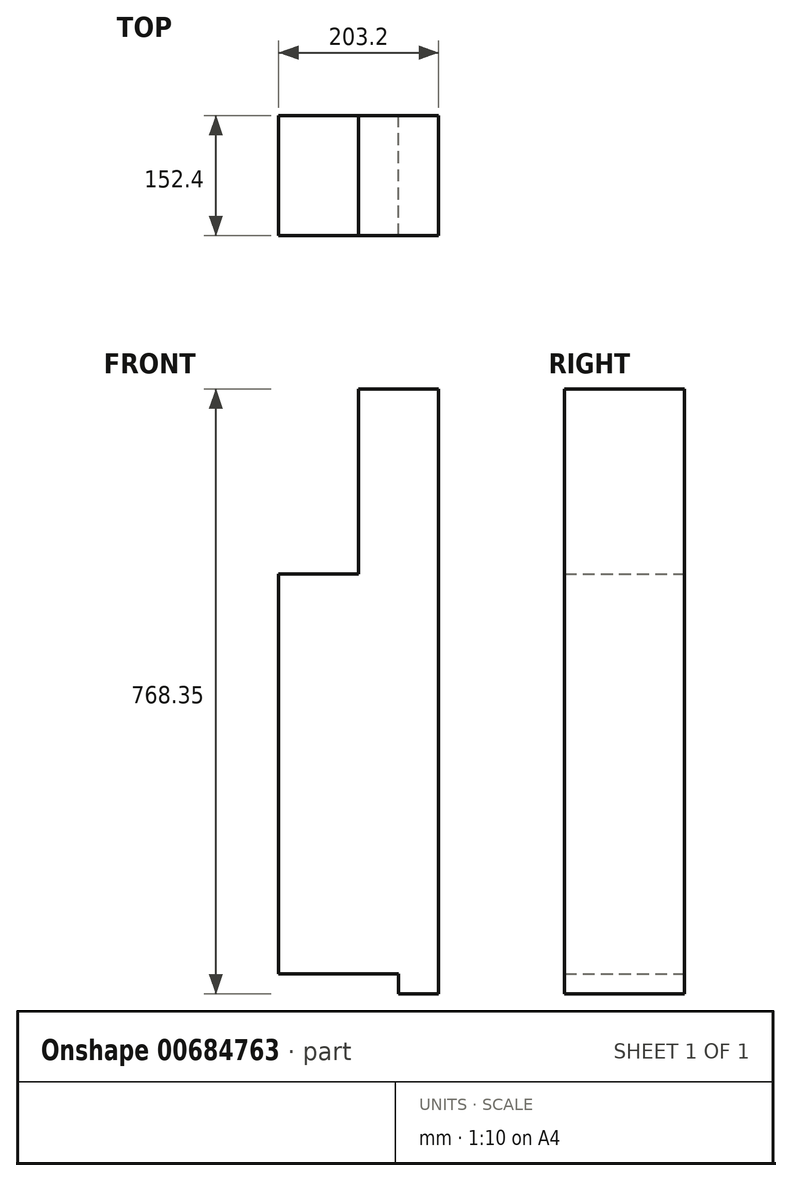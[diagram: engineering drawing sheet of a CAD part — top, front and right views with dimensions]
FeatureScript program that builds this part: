
annotation { "Feature Type Name" : "Feature", "Feature Type Description" : "" }
export const myFeature = defineFeature(function(context is Context, id is Id, definition is map)
    precondition{}
    {
        {
            var Q0;
            Q0=qCreatedBy(makeId("Front.planeOp"),FACE);
            var sketch = newSketch(context, id + "F0", { "sketchPlane" : qUnion([Q0])});
            skLineSegment(sketch, "E0", {"start": v(-152.4, 0) * mm, "end": v(-152.4, 508) * mm});
            skLineSegment(sketch, "E1", {"start": v(-50.8, 742.95) * mm, "end": v(50.8, 742.95) * mm});
            skLineSegment(sketch, "E2", {"start": v(50.8, 742.95) * mm, "end": v(50.8, -25.4) * mm});
            skLineSegment(sketch, "E3", {"start": v(50.8, -25.4) * mm, "end": v(0, -25.4) * mm});
            skLineSegment(sketch, "E4", {"start": v(0, -25.4) * mm, "end": v(0, 0) * mm});
            skLineSegment(sketch, "E5", {"start": v(0, 0) * mm, "end": v(-152.4, 0) * mm});
            skLineSegment(sketch, "E6", {"start": v(-50.8, 742.95) * mm, "end": v(-50.8, 508) * mm});
            skLineSegment(sketch, "E7", {"start": v(-50.8, 508) * mm, "end": v(-152.4, 508) * mm});
            skSolve(sketch);
        }
        {
            var Q0;
            Q0=qSketchRegion(id+"F0",true);
            extrude(context, id + "F1", {"entities" : qUnion([Q0]), "endBound" : BoundingType.SYMMETRIC, "depth" : 152.4 * mm, "offsetDistance" : 25.4 * mm});
        }
    });
